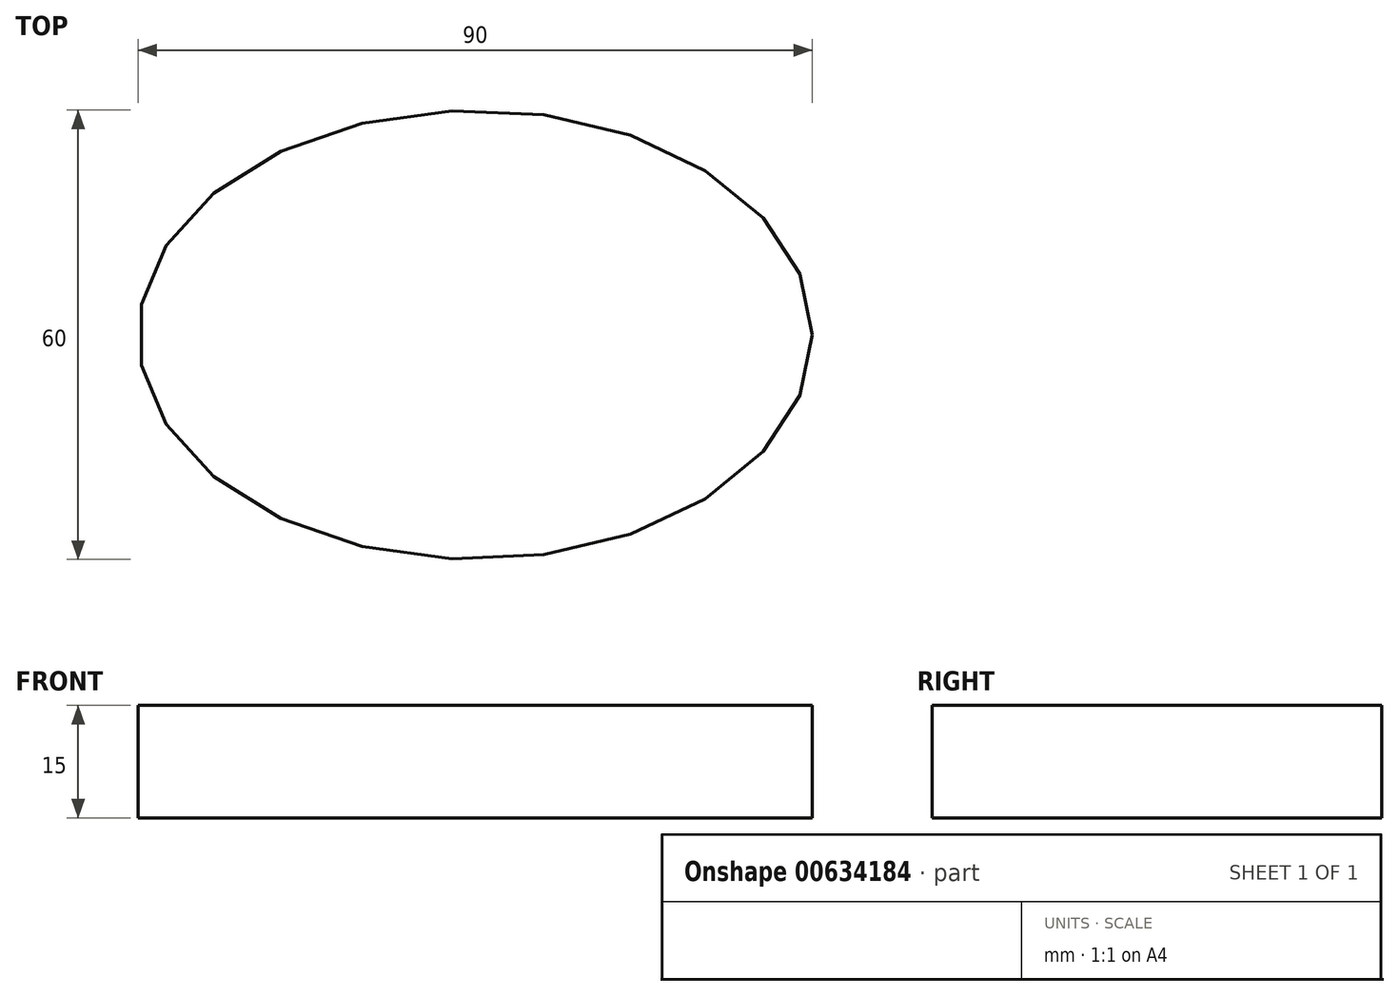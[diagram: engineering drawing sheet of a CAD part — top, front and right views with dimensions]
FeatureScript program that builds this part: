
annotation { "Feature Type Name" : "Feature", "Feature Type Description" : "" }
export const myFeature = defineFeature(function(context is Context, id is Id, definition is map)
    precondition{}
    {
        {
            var Q0;
            Q0=qCreatedBy(makeId("Top.planeOp"),FACE);
            var sketch = newSketch(context, id + "F0", { "sketchPlane" : qUnion([Q0])});
            skEllipse(sketch, "E0", {"center": v(0, 0) * mm, "majorRadius": 45 * mm, "minorRadius": 30 * mm, "majorAxis": v(1, 0)});
            skFitSpline(sketch, "E1.0", {"points": [v(46.96, -1.64) * mm, v(47.02, 0) * mm, v(46.96, 1.64) * mm, v(46.72, 3.8) * mm, v(46.12, 6.47) * mm, v(44.95, 9.57) * mm, v(43.34, 12.56) * mm, v(41.33, 15.4) * mm, v(38.92, 18.09) * mm, v(36.6, 20.18) * mm, v(34.56, 21.75) * mm, v(32.94, 22.89) * mm, v(31.25, 23.96) * mm, v(28.9, 25.3) * mm, v(25.81, 26.83) * mm, v(21.9, 28.4) * mm, v(17.78, 29.69) * mm, v(13.5, 30.71) * mm, v(9.1, 31.45) * mm, v(5.34, 31.82) * mm, v(2.3, 31.97) * mm, v(0, 32.01) * mm, v(-2.3, 31.97) * mm, v(-5.34, 31.82) * mm, v(-9.1, 31.45) * mm, v(-13.5, 30.71) * mm, v(-17.78, 29.69) * mm, v(-21.9, 28.4) * mm, v(-25.81, 26.83) * mm, v(-28.9, 25.3) * mm, v(-31.25, 23.96) * mm, v(-32.94, 22.89) * mm, v(-34.56, 21.75) * mm, v(-36.6, 20.18) * mm, v(-38.92, 18.09) * mm, v(-41.33, 15.4) * mm, v(-43.34, 12.56) * mm, v(-44.95, 9.57) * mm, v(-46.12, 6.47) * mm, v(-46.72, 3.8) * mm, v(-46.96, 1.64) * mm, v(-47.02, 0) * mm, v(-46.96, -1.64) * mm, v(-46.72, -3.8) * mm, v(-46.12, -6.47) * mm, v(-44.95, -9.57) * mm, v(-43.34, -12.56) * mm, v(-41.33, -15.4) * mm, v(-38.92, -18.09) * mm, v(-36.6, -20.18) * mm, v(-34.56, -21.75) * mm, v(-32.94, -22.89) * mm, v(-31.25, -23.96) * mm, v(-28.9, -25.3) * mm, v(-25.81, -26.83) * mm, v(-21.9, -28.4) * mm, v(-17.78, -29.69) * mm, v(-13.5, -30.71) * mm, v(-9.1, -31.45) * mm, v(-5.34, -31.82) * mm, v(-2.3, -31.97) * mm, v(0, -32.01) * mm, v(2.3, -31.97) * mm, v(5.34, -31.82) * mm, v(9.1, -31.45) * mm, v(13.5, -30.71) * mm, v(17.78, -29.69) * mm, v(21.9, -28.4) * mm, v(25.81, -26.83) * mm, v(28.9, -25.3) * mm, v(31.25, -23.96) * mm, v(32.94, -22.89) * mm, v(34.56, -21.75) * mm, v(36.6, -20.18) * mm, v(38.92, -18.09) * mm, v(41.33, -15.4) * mm, v(43.34, -12.56) * mm, v(44.95, -9.57) * mm, v(46.12, -6.47) * mm, v(46.72, -3.8) * mm, v(46.96, -1.64) * mm, v(47.02, 0) * mm, v(46.96, 1.64) * mm, v(46.96, -1.64) * mm]});
            skSolve(sketch);
        }
        {
            var Q0;
            Q0 = qSketchRegion(id + "F0", true);
            extrude(context, id + "F1", {"entities" : qUnion([Q0]), "depth" : 15 * mm, "offsetDistance" : 25 * mm});
        }
    });
